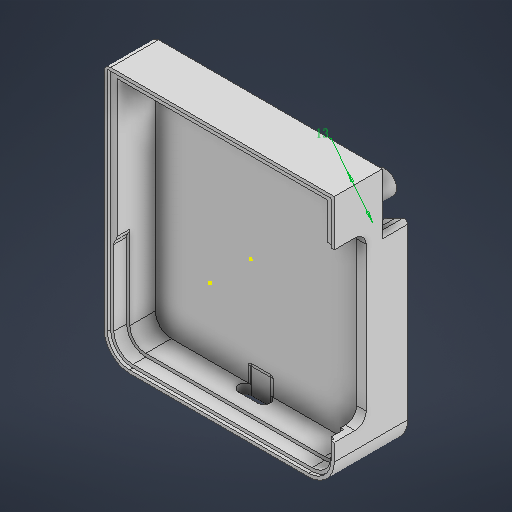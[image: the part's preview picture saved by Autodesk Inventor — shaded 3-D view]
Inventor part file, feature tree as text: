
AUTODESK INVENTOR PART (.ipt)
format: ipt  version: 2025 (Build 290162000, 162)  size: 398,848 bytes
history: native  units: mm
features: other x15, sketch x14, extrude x9, fillet x7, reference x3, chamfer x1, projected_geometry x1
ambient origin geometry x8: Origin, YZ Plane, XZ Plane, XY Plane, X Axis, Y Axis, Z Axis, Center Point
bodies: 实体1 (feature_tree)
feature tree (50):
  sketch  "草图1"  dims[d3=2.0mm d4=0.0mm d5=15.0mm d6=0.0mm]
  extrude  "拉伸1"  Depth=15.0mm TaperAngle=0.0deg
  extrude  "拉伸2"  Depth=1.0mm
  sketch  "草图3"  dims[d11=7.0mm d12=1.0mm]
  sketch  "草图5"  dims[d13=2.0mm d14=91.25mm d15=0.0mm d17=2.0mm]
  extrude  "拉伸4"  Depth=2.0mm TaperAngle=0.0deg
  other  "直接编辑1"
  fillet  "圆角2"  Radius=2.0mm
  sketch  "草图6"  dims[d18=4.0mm d19=10.0mm d20=10.0mm]
  extrude  "拉伸5"  Depth=10.0mm
  fillet  "圆角3"  Radius=10.0mm
  extrude  "拉伸6"  Depth=1.0mm
  fillet  "圆角4"  Radius=1.0mm
  other  "直接编辑2"
  extrude  "拉伸7"  Depth=3.0mm
  chamfer  "倒角2"  Distance=1.5mm
  other  "直接编辑3"
  other  "直接编辑4"
  fillet  "圆角6"  Radius=16.0mm
  extrude  "拉伸9"  Depth=1.0mm
  fillet  "圆角7"  Radius=4.0mm
  sketch  "草图12"  dims[d44=2.0mm d45=7.0mm]
  extrude  "拉伸10"  Depth=2.0mm
  extrude  "拉伸11"  Depth=1.0mm
  fillet  "圆角8"  Radius=11.0mm
  sketch  "草图15"  dims[d53=1.0mm]
  sketch  "草图16"  dims[d54=1.0mm]
  fillet  "圆角9"  Radius=1.0mm
  sketch  "草图17"  dims[d55=13.0mm]
  other  "直接编辑5"
  reference  "参考2"
  sketch  "草图7"  dims[d21=0.0mm d25=8.75mm d26=1.0mm d27=0.0mm]
  sketch  "草图8"  dims[d28=0.2mm d29=3.0mm d30=1.5mm d31=0.0mm]
  reference  "参考3"
  sketch  "草图9"  dims[d32=1.0mm d33=2.0mm d34=45.0deg d36=16.0mm]
  sketch  "草图11"  dims[d40=8.0mm d41=1.0mm d42=4.0mm d43=0.0mm]
  sketch  "草图13"  dims[d46=8.0mm d47=0.0mm d48=7.0mm d49=11.0mm d50=1.0mm]
  sketch  "草图14"  dims[d51=8.0mm d52=0.0mm]
  reference  "参考4"
  projected_geometry  "投影回路1"
  parser-record x1  (decoder bookkeeping rows leaked as tree rows — omitted from the tree; the rows remain in map.json)
  other  "装配体.iam"
  other  "屏幕:1"
  other  "删除1"
  other  "删除2"
  other  "删除3"
  other  "删除4"
  other  "删除5"
  other  "部件1:1"
  other  "真键盘外壳:1"
note: 1 file-system path scrubbed to <path> (originals preserved in map.json)
